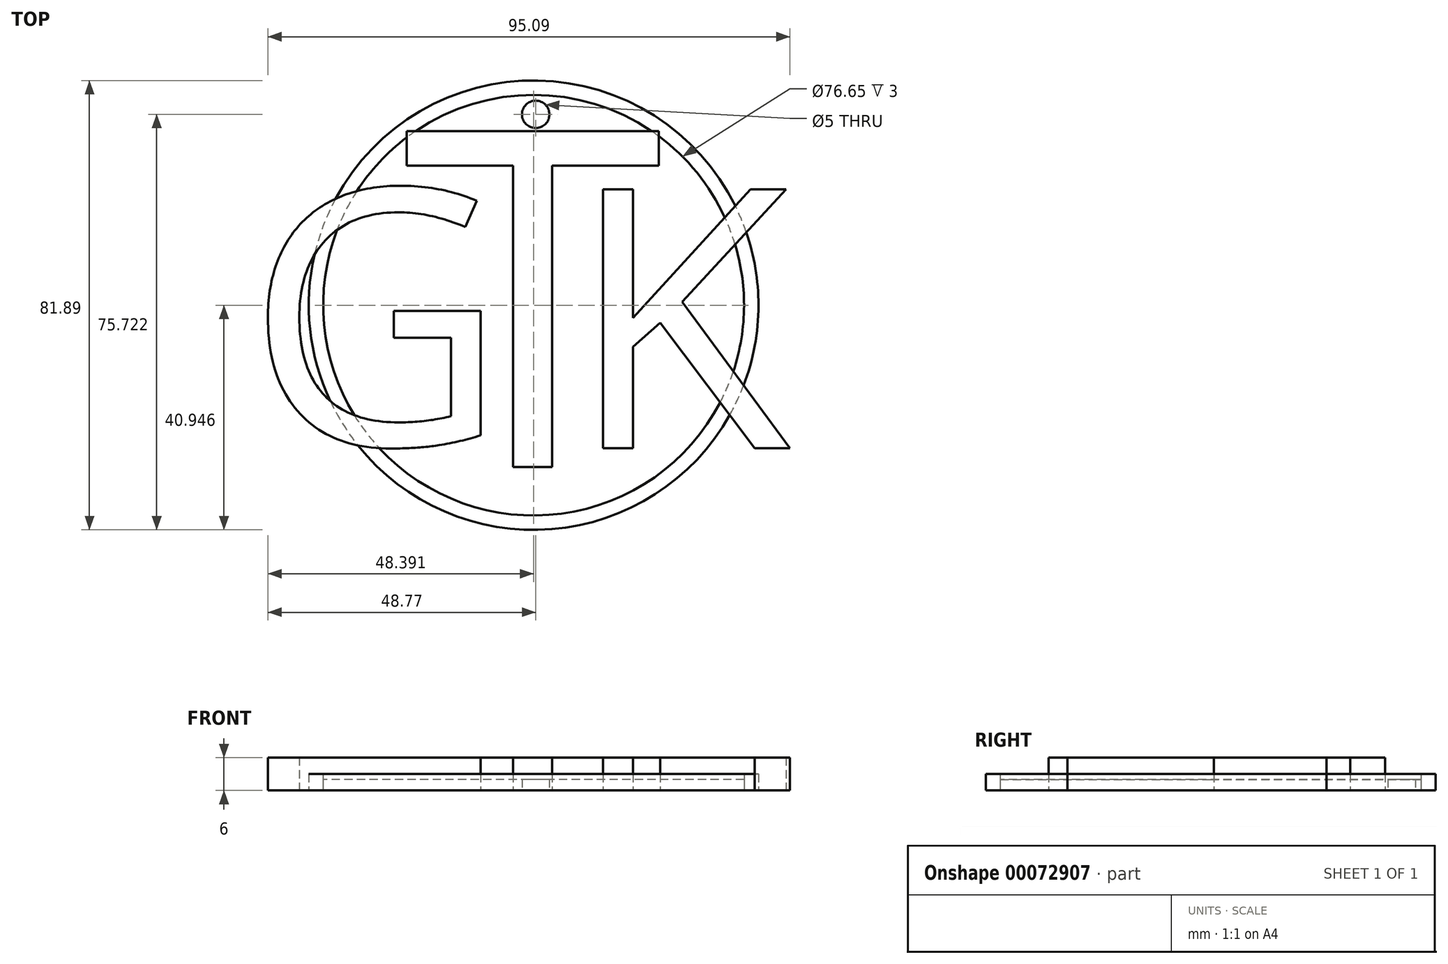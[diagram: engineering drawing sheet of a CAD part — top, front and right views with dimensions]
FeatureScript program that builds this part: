
annotation { "Feature Type Name" : "Feature", "Feature Type Description" : "" }
export const myFeature = defineFeature(function(context is Context, id is Id, definition is map)
    precondition{}
    {
        {
            var Q0;
            Q0=qCreatedBy(makeId("Top.planeOp"),FACE);
            var sketch = newSketch(context, id + "F0", { "sketchPlane" : qUnion([Q0])});
            skText(sketch, "E0", { "text": "G", "fontName": "OpenSans-Regular.ttf"});
            skText(sketch, "E1", { "text": "T", "fontName": "OpenSans-Regular.ttf"});
            skText(sketch, "E2", { "text": "K", "fontName": "OpenSans-Regular.ttf"});
            const initialGuessF0  = {"E0": [-0.05276, -0.03215, 1, 0, 0.04698], "E1": [-0.02426, -0.0362, 1, 0, 0.0618], "E2": [0.00578, -0.03273, 1, 0, 0.04756]};
            skSetInitialGuess(sketch, initialGuessF0);
            skSolve(sketch);
        }
        {
            var Q0;
            Q0 = qSketchRegion(id + "F0", true);
            var Q1;
            Q1=makeQuery(id+"F0.imprint","IMPRINT",FACE,{"disambiguationData":[TD([[makeQuery(id+"F0.imprint","IMPRINT",EDGE,{"derivedFrom":sQuery(id+"F0.wireOp",EDGE,"E1.sketch_text.stroke-0")}),-1.0]])]});
            extrude(context, id + "F1", {"entities" : qUnion([Q0, Q1]), "depth" : 6 * mm});
        }
        {
            var Q0;
            Q0=qCreatedBy(makeId("Top.planeOp"),FACE);
            var sketch = newSketch(context, id + "F2", { "sketchPlane" : qUnion([Q0])});
            skCircle(sketch, "E3", {"center": v(-74.48, 97.7) * mm, "radius": 40.95 * mm});
            skCircle(sketch, "E4.0", {"center": v(-74.48, 97.7) * mm, "radius": 38.32 * mm});
            skSolve(sketch);
        }
        {
            var Q0;
            Q0=makeQuery(id+"F2.imprint","IMPRINT",FACE,{"disambiguationData":[TD([[makeQuery(id+"F2.imprint","IMPRINT",EDGE,{"derivedFrom":sQuery(id+"F2.wireOp",EDGE,"E3")}),1.0]])]});
            extrude(context, id + "F3", {"entities" : qUnion([Q0]), "depth" : 3 * mm});
        }
        {
            var Q0;
            Q0=makeQuery(id+"F2.imprint","IMPRINT",FACE,{"disambiguationData":[TD([[makeQuery(id+"F2.imprint","IMPRINT",EDGE,{"derivedFrom":sQuery(id+"F2.wireOp",EDGE,"E4.0")}),1.0]])]});
            extrude(context, id + "F4", {"entities" : qUnion([Q0]), "depth" : 2 * mm});
        }
        {
            var Q0;
            Q0=makeQuery(id+"F3.opExtrude","SWEPT_BODY",BODY,{"disambiguationData":[OSD([sQuery(id+"F2.wireOp",EDGE,"E3")])]});
            transform(context, id + "F5", {"entities" : qUnion([Q0]), "transformType" : TransformType.TRANSLATION_3D, "dx" : 74.1 * mm, "dy" : -104.36 * mm, "dz" : 0 * mm, "makeCopy" : false});
        }
        {
            var Q0;
            Q0=makeQuery(id+"F4.opExtrude","SWEPT_BODY",BODY,{"disambiguationData":[OSD([sQuery(id+"F2.wireOp",EDGE,"E4.0")])]});
            transform(context, id + "F6", {"entities" : qUnion([Q0]), "transformType" : TransformType.TRANSLATION_3D, "dx" : 74.1 * mm, "dy" : -104.36 * mm, "dz" : 0 * mm, "makeCopy" : false});
        }
        {
            var Q0;
            Q0=qCreatedBy(makeId("Top.planeOp"),FACE);
            var sketch = newSketch(context, id + "F7", { "sketchPlane" : qUnion([Q0])});
            skCircle(sketch, "E5", {"center": v(0, 28.1) * mm, "radius": 2.5 * mm});
            skSolve(sketch);
        }
        {
            var Q0;
            Q0 = qSketchRegion(id + "F7", true);
            var Q1;
            Q1=sQuery(id+"F7.wireOp",EDGE,"E5");
            extrude(context, id + "F8", {"entities" : qUnion([Q0]), "surfaceEntities" : qUnion([Q1]), "endBound" : BoundingType.SYMMETRIC, "depth" : 25 * mm});
        }
        {
            var Q0;
            Q0=makeQuery(id+"F8.opExtrude","SWEPT_BODY",BODY,{"disambiguationData":[OSD([sQuery(id+"F7.wireOp",EDGE,"E5")])]});
            var Q1;
            Q1=makeQuery(id+"F4.opExtrude","SWEPT_BODY",BODY,{"disambiguationData":[OSD([sQuery(id+"F2.wireOp",EDGE,"E4.0")])]});
            booleanBodies(context, id + "F9", {"operationType" : BooleanOperationType.SUBTRACTION, "tools" : qUnion([Q0]), "targets" : qUnion([Q1])});
        }
    });
